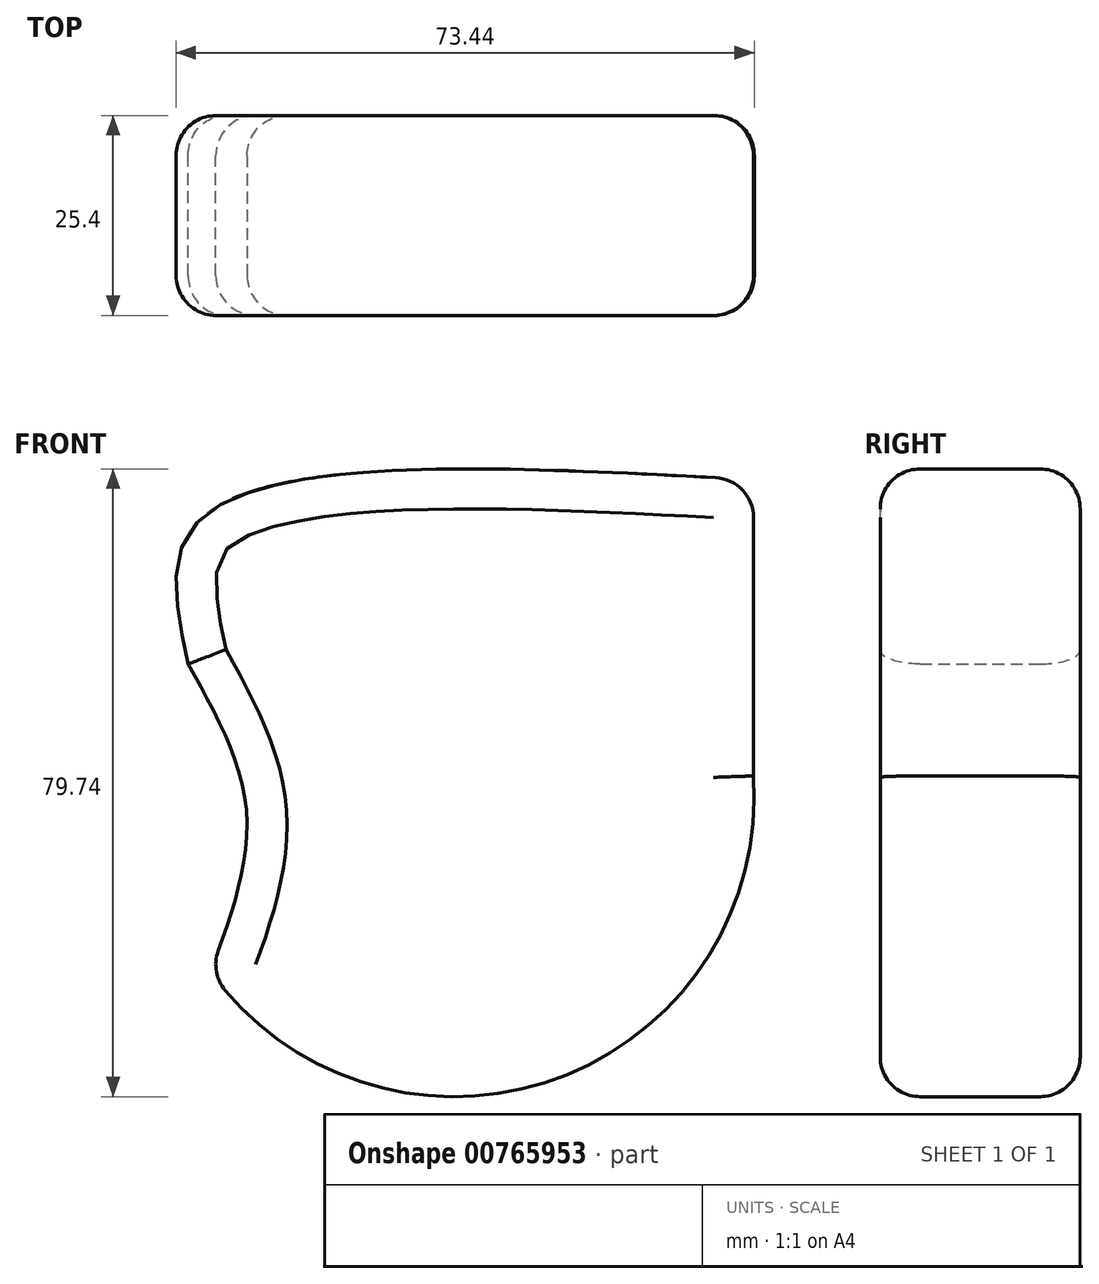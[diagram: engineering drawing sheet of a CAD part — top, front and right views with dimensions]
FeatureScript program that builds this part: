
annotation { "Feature Type Name" : "Feature", "Feature Type Description" : "" }
export const myFeature = defineFeature(function(context is Context, id is Id, definition is map)
    precondition{}
    {
        {
            var Q0;
            Q0=qCreatedBy(makeId("Front.planeOp"),FACE);
            var sketch = newSketch(context, id + "F0", { "sketchPlane" : qUnion([Q0])});
            skArc(sketch, "E0", {"start": v(-30.95, -22.22) * mm, "mid": v(12.92, -35.84) * mm, "end": v(38, 2.65) * mm});
            skLineSegment(sketch, "E1", {"start": v(38, 2.65) * mm, "end": v(38, 34.34) * mm});
            skFitSpline(sketch, "E2", {"points": [v(-30.95, -22.22) * mm, v(-26.39, -1.89) * mm, v(-33.82, 16.86) * mm], "startDerivative": vector(15.1, 40.97) * mm, "endDerivative": vector(-20.93, 37.2) * mm});
            skFitSpline(sketch, "E3", {"points": [v(-33.82, 16.86) * mm, v(-32.46, 35.1) * mm, v(40.49, 40.13) * mm], "startDerivative": vector(-13.48, 62.58) * mm, "endDerivative": vector(144.55, -8.18) * mm});
            skLineSegment(sketch, "E4", {"start": v(38, 34.34) * mm, "end": v(38, 40.27) * mm});
            skSolve(sketch);
        }
        {
            var Q0;
            Q0 = qSketchRegion(id + "F0", true);
            extrude(context, id + "F1", {"entities" : qUnion([Q0]), "depth" : 25.4 * mm, "offsetDistance" : 25.4 * mm});
        }
        {
            var Q0;
            Q0=makeQuery(id+"F1.opExtrude","CAP_EDGE",EDGE,{"disambiguationData":[OSD([sQuery(id+"F0.wireOp",EDGE,"E3")])],"isStart":false});
            var Q1;
            Q1=makeQuery(id+"F1.opExtrude","CAP_EDGE",EDGE,{"disambiguationData":[OSD([sQuery(id+"F0.wireOp",EDGE,"E2")])],"isStart":false});
            var Q2;
            Q2=makeQuery(id+"F1.opExtrude","CAP_EDGE",EDGE,{"disambiguationData":[OSD([sQuery(id+"F0.wireOp",EDGE,"E0")])],"isStart":false});
            var Q3;
            Q3=makeQuery(id+"F1.opExtrude","SWEPT_EDGE",EDGE,{"disambiguationData":[OSD([sQuery(id+"F0.wireOp",EDGE,"E3"),sQuery(id+"F0.wireOp",EDGE,"E4")])]});
            var Q4;
            Q4=makeQuery(id+"F1.opExtrude","CAP_EDGE",EDGE,{"disambiguationData":[OSD([sQuery(id+"F0.wireOp",EDGE,"E3")])],"isStart":true});
            var Q5;
            Q5=makeQuery(id+"F1.opExtrude","CAP_EDGE",EDGE,{"disambiguationData":[OSD([sQuery(id+"F0.wireOp",EDGE,"E1"),sQuery(id+"F0.wireOp",EDGE,"E4")])],"isStart":true});
            var Q6;
            Q6=makeQuery(id+"F1.opExtrude","CAP_EDGE",EDGE,{"disambiguationData":[OSD([sQuery(id+"F0.wireOp",EDGE,"E2")])],"isStart":true});
            var Q7;
            Q7=makeQuery(id+"F1.opExtrude","CAP_EDGE",EDGE,{"disambiguationData":[OSD([sQuery(id+"F0.wireOp",EDGE,"E0")])],"isStart":true});
            var Q8;
            Q8=makeQuery(id+"F1.opExtrude","SWEPT_EDGE",EDGE,{"disambiguationData":[OSD([sQuery(id+"F0.wireOp",EDGE,"E0"),sQuery(id+"F0.wireOp",EDGE,"E2")])]});
            fillet(context, id + "F2", {"entities" : qUnion([Q0, Q1, Q2, Q3, Q4, Q5, Q6, Q7, Q8]), "radius" : 5.08 * mm, "tangentPropagation" : true, "allowEdgeOverflow" : false});
        }
    });
